# Revit family: Sanitary_Compound-Units_hansgrohe_54289XXX-Xilesa-E-Furniture-feet_145-20_2-pieces
name_source: partatom
category: Furniture
units: mm (PartAtom-declared; Revit-internal decimal feet)

## family parameters
Cut with Voids When Loaded = No
Host = Face
OmniClass Number = 23.21.19.15.33.13
OmniClass Title = Residential Bathroom Specialty Casework
Render Appearance Source = Family Geometry
Room Calculation Point = No
Shared = No

## types (1)
- 670 Matt Black
    Default Elevation = 0 mm  [stored 0 ft]
    Description = Xilesa E Furniture feet 145/20, 2 pieces
    Height = 0 mm  [stored 0 ft]
    Manufacturer = Hansgrohe
    Material 1 = Hansgrohe - Metal - 670 Matte Black
    Material 2 = Hansgrohe - Plastic - Black
    Model = 54289XXX
    Product Page URL = https://www.hansgrohe.com
    Product data url = https://www.bimobject.com
    URL = https://www.hansgrohe.com
    Version = 1

note: [stored X ft] marks values corroborated as IEEE doubles in the binary element streams (Revit-internal decimal feet)

## geometry (parser evidence)
native form markers: Sweep x3
no freeform markers — native parametric forms only
